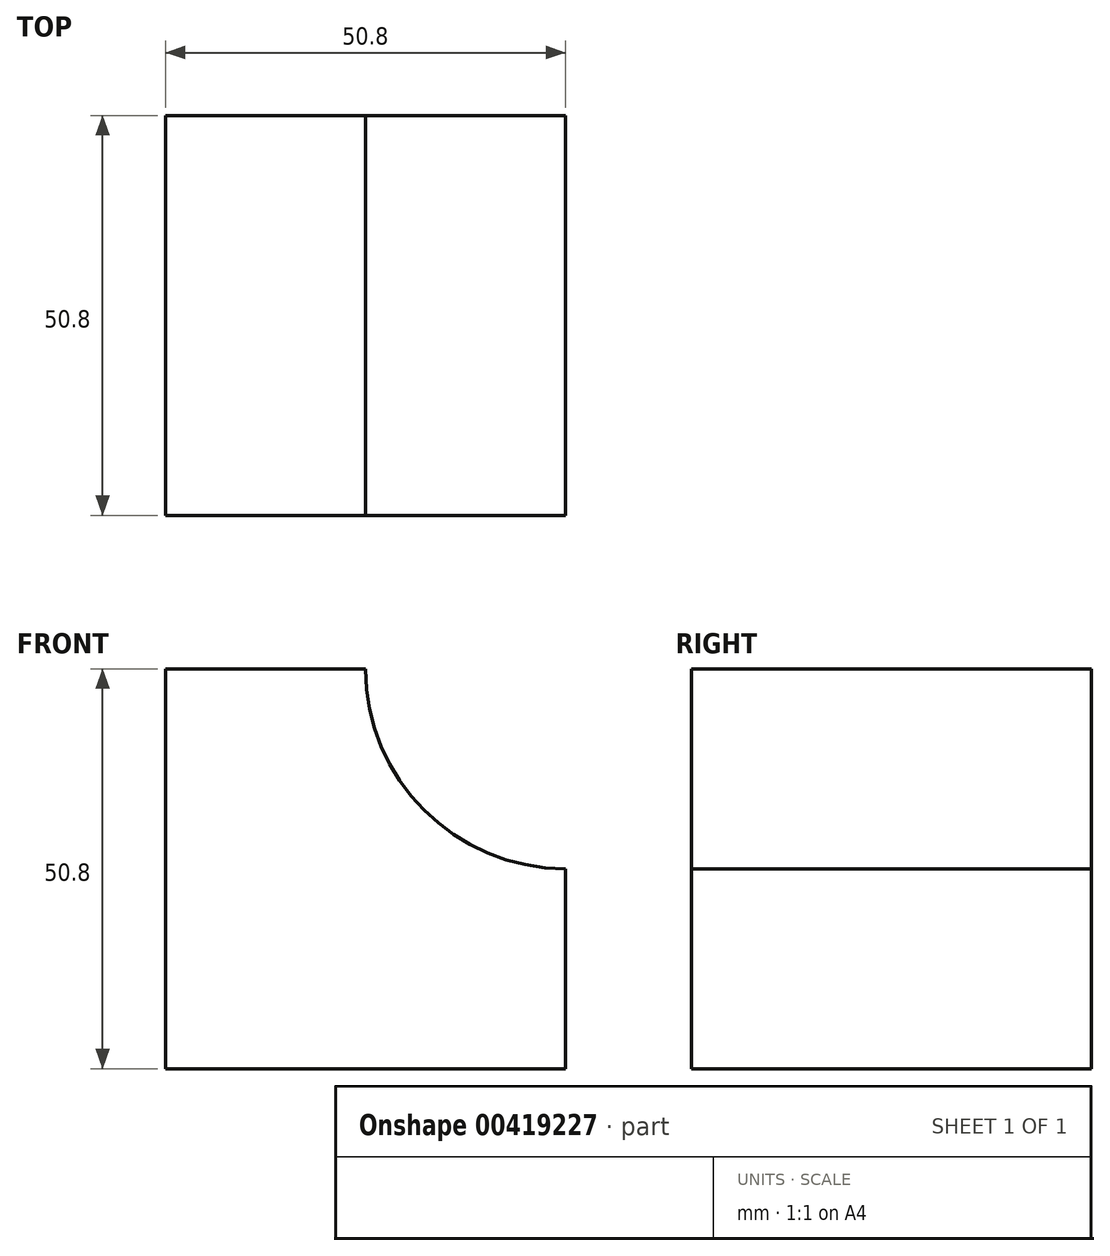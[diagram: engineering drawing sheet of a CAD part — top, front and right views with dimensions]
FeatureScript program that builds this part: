
annotation { "Feature Type Name" : "Feature", "Feature Type Description" : "" }
export const myFeature = defineFeature(function(context is Context, id is Id, definition is map)
    precondition{}
    {
        {
            var Q0;
            Q0=qCreatedBy(makeId("Front.planeOp"),FACE);
            var sketch = newSketch(context, id + "F0", { "sketchPlane" : qUnion([Q0])});
            skLineSegment(sketch, "E0", {"start": v(0, 0) * mm, "end": v(-50.8, 0) * mm});
            skLineSegment(sketch, "E1", {"start": v(-50.8, 0) * mm, "end": v(-50.8, 50.8) * mm});
            skLineSegment(sketch, "E2", {"start": v(-50.8, 50.8) * mm, "end": v(-25.4, 50.8) * mm});
            skArc(sketch, "E3", {"start": v(-25.4, 50.8) * mm, "mid": v(-17.96, 32.84) * mm, "end": v(0, 25.4) * mm});
            skLineSegment(sketch, "E4", {"start": v(0, 25.4) * mm, "end": v(0, 0) * mm});
            skSolve(sketch);
        }
        {
            var Q0;
            Q0=makeQuery(id+"F0.imprint","IMPRINT",FACE,{"disambiguationData":[TD([[makeQuery(id+"F0.imprint","IMPRINT",EDGE,{"derivedFrom":sQuery(id+"F0.wireOp",EDGE,"E0")}),-1.0]])]});
            extrude(context, id + "F1", {"entities" : qUnion([Q0]), "depth" : 50.8 * mm});
        }
    });
